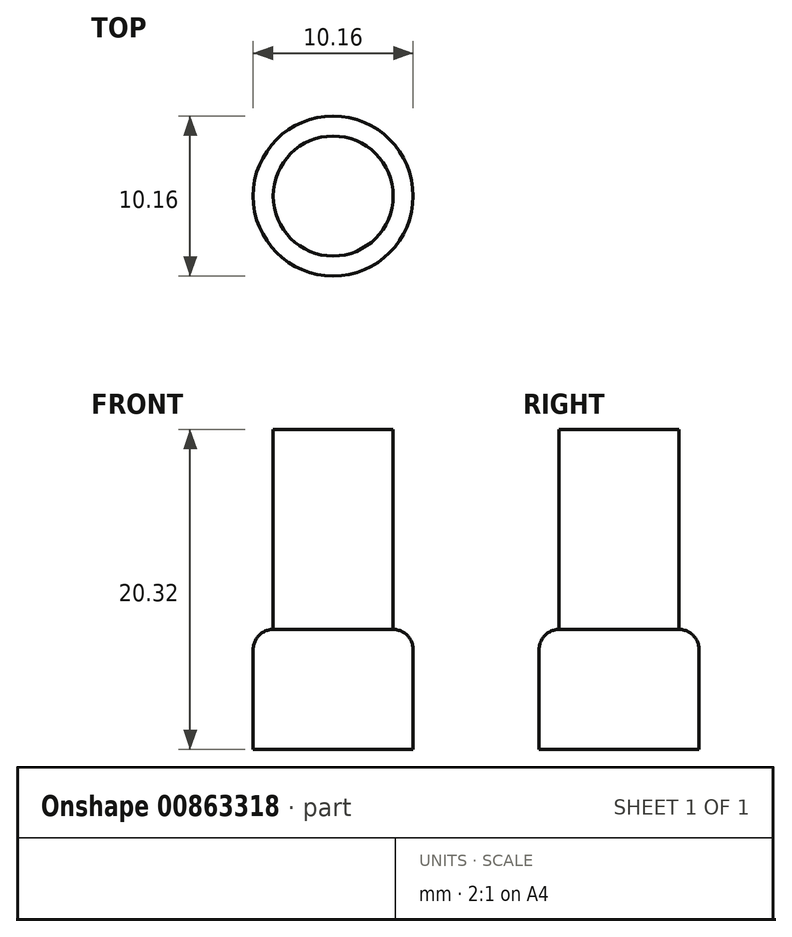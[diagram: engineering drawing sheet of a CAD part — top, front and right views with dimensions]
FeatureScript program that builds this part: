
annotation { "Feature Type Name" : "Feature", "Feature Type Description" : "" }
export const myFeature = defineFeature(function(context is Context, id is Id, definition is map)
    precondition{}
    {
        {
            var Q0;
            Q0=qCreatedBy(makeId("Top.planeOp"),FACE);
            var sketch = newSketch(context, id + "F0", { "sketchPlane" : qUnion([Q0])});
            skCircle(sketch, "E0", {"center": v(0, 0) * mm, "radius": 5.08 * mm});
            skSolve(sketch);
        }
        {
            var Q0;
            Q0=makeQuery(id+"F0.imprint","IMPRINT",FACE,{"disambiguationData":[TD([[makeQuery(id+"F0.imprint","IMPRINT",EDGE,{"derivedFrom":sQuery(id+"F0.wireOp",EDGE,"E0")}),1.0]])]});
            extrude(context, id + "F1", {"entities" : qUnion([Q0]), "depth" : 7.62 * mm, "offsetDistance" : 25.4 * mm});
        }
        {
            var Q0;
            Q0=makeQuery(id+"F1.opExtrude","CAP_EDGE",EDGE,{"disambiguationData":[OSD([sQuery(id+"F0.wireOp",EDGE,"E0")])],"isStart":false});
            fillet(context, id + "F2", {"entities" : qUnion([Q0]), "radius" : 1.27 * mm, "tangentPropagation" : true, "allowEdgeOverflow" : false});
        }
        {
            var Q0;
            Q0=makeQuery(id+"F1.opExtrude","CAP_FACE",FACE,{"disambiguationData":[OSD([sQuery(id+"F0.wireOp",EDGE,"E0")])],"isStart":false});
            extrude(context, id + "F3", {"entities" : qUnion([Q0]), "operationType" : NewBodyOperationType.ADD, "depth" : 12.7 * mm, "offsetDistance" : 25.4 * mm});
        }
    });
